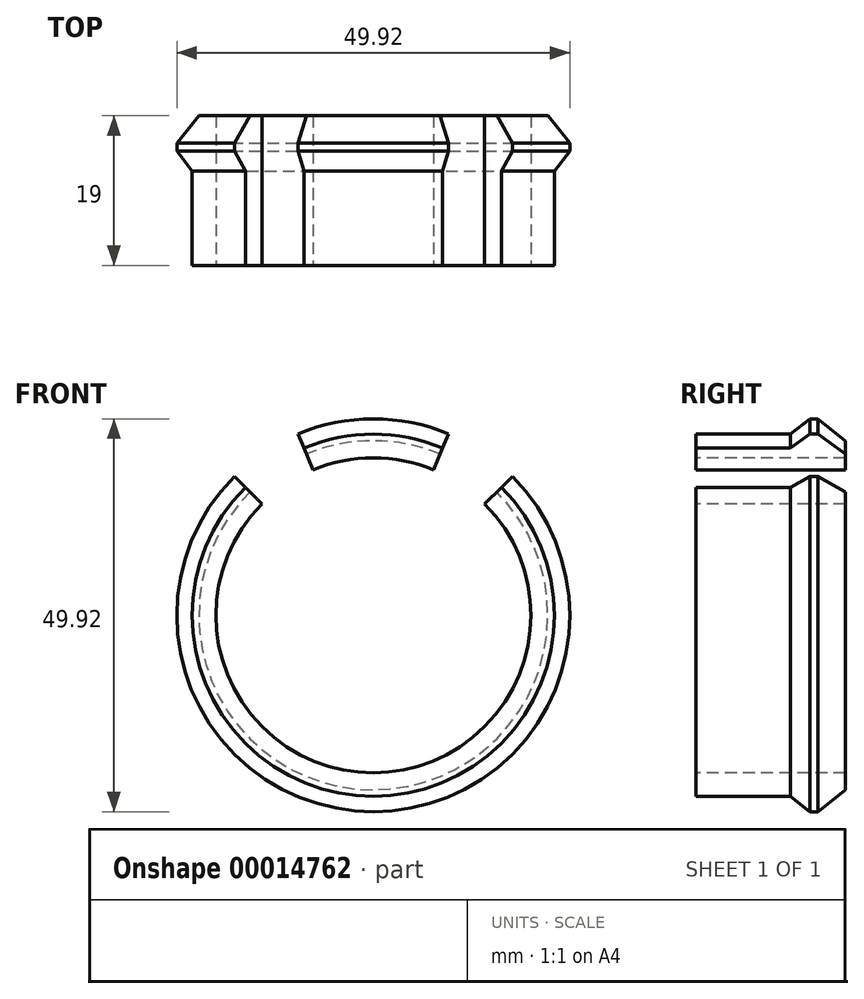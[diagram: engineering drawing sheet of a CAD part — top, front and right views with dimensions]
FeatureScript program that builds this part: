
annotation { "Feature Type Name" : "Feature", "Feature Type Description" : "" }
export const myFeature = defineFeature(function(context is Context, id is Id, definition is map)
    precondition{}
    {
        {
            var Q0;
            Q0=qCreatedBy(makeId("Top.planeOp"),FACE);
            var sketch = newSketch(context, id + "F0", { "sketchPlane" : qUnion([Q0])});
            skLineSegment(sketch, "E0", {"start": v(-8, 0) * mm, "end": v(-8, 19) * mm});
            skLineSegment(sketch, "E1", {"start": v(-8, 19) * mm, "end": v(-5.83, 19) * mm});
            skLineSegment(sketch, "E2", {"start": v(-5.83, 19) * mm, "end": v(-3.04, 15.5) * mm});
            skLineSegment(sketch, "E3", {"start": v(-3.04, 15.5) * mm, "end": v(-3.04, 14.5) * mm});
            skLineSegment(sketch, "E4", {"start": v(-3.04, 14.5) * mm, "end": v(-5, 12) * mm});
            skLineSegment(sketch, "E5", {"start": v(-5, 12) * mm, "end": v(-5, 0) * mm});
            skLineSegment(sketch, "E6", {"start": v(-5, 0) * mm, "end": v(-8, 0) * mm});
            skSolve(sketch);
        }
        {
            var Q0;
            Q0=qCreatedBy(makeId("Front.planeOp"),FACE);
            var sketch = newSketch(context, id + "F1", { "sketchPlane" : qUnion([Q0])});
            skCircle(sketch, "E7", {"center": v(-28, 0) * mm, "radius": 23 * mm});
            skSolve(sketch);
        }
        {
            var Q0;
            Q0=makeQuery(id+"F0.imprint","IMPRINT",FACE,{"disambiguationData":[TD([[makeQuery(id+"F0.imprint","IMPRINT",EDGE,{"derivedFrom":sQuery(id+"F0.wireOp",EDGE,"E0")}),-1.0]])]});
            var Q1;
            Q1=sQuery(id+"F1.wireOp",EDGE,"E7");
            sweep(context, id + "F2", {"profiles" : qUnion([Q0]), "path" : qUnion([Q1])});
        }
        {
            var Q0;
            Q0=makeQuery(id+"F2.opSweep","SWEPT_FACE",FACE,{"disambiguationData":[OSD([sQuery(id+"F0.wireOp",EDGE,"E1"),sQuery(id+"F1.wireOp",EDGE,"E7")])]});
            cPlane(context, id + "F3", {"entities" : qUnion([Q0]), "cplaneType" : CPlaneType.OFFSET, "offset" : 0 * mm, "width" : 150 * mm, "height" : 150 * mm});
        }
        {
            var Q0;
            Q0=qCreatedBy(id+"F3.planeOp",FACE);
            var sketch = newSketch(context, id + "F4", { "sketchPlane" : qUnion([Q0])});
            skPoint(sketch, "E8", {"position": v(28, 0) * mm});
            skLineSegment(sketch, "E9", {"start": v(28, 0) * mm, "end": v(28, 26.4) * mm});
            skLineSegment(sketch, "E10", {"start": v(28, 0) * mm, "end": v(8.37, 19.63) * mm});
            skLineSegment(sketch, "E11", {"start": v(28, 0) * mm, "end": v(46.78, 18.78) * mm});
            skLineSegment(sketch, "E12", {"start": v(28, 0) * mm, "end": v(38.28, 24.81) * mm});
            skLineSegment(sketch, "E13", {"start": v(28, 0) * mm, "end": v(17.75, 24.74) * mm});
            skLineSegment(sketch, "E14", {"start": v(46.78, 18.78) * mm, "end": v(38.28, 24.81) * mm});
            skLineSegment(sketch, "E15", {"start": v(17.75, 24.74) * mm, "end": v(8.37, 19.63) * mm});
            skSolve(sketch);
        }
        {
            var Q0;
            Q0=makeQuery(id+"F4.imprint","IMPRINT",FACE,{"disambiguationData":[TD([[makeQuery(id+"F4.imprint","IMPRINT",EDGE,{"derivedFrom":sQuery(id+"F4.wireOp",EDGE,"E11")}),1.0]])]});
            var Q1;
            Q1=makeQuery(id+"F4.imprint","IMPRINT",FACE,{"disambiguationData":[TD([[makeQuery(id+"F4.imprint","IMPRINT",EDGE,{"derivedFrom":sQuery(id+"F4.wireOp",EDGE,"E10")}),-1.0]])]});
            extrude(context, id + "F5", {"entities" : qUnion([Q0, Q1]), "operationType" : NewBodyOperationType.REMOVE, "oppositeDirection" : true, "depth" : 25 * mm});
        }
    });
